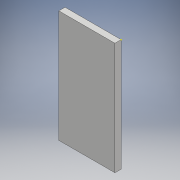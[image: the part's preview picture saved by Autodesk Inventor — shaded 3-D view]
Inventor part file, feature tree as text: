
AUTODESK INVENTOR PART (.ipt)
format: ipt  version: 2017 SP1 (Build 210196100, 196)  size: 90,112 bytes
history: native  units: mm
features: sketch x2, extrude x1
ambient origin geometry x8: Origin, YZ Plane, XZ Plane, XY Plane, X Axis, Y Axis, Z Axis, Center Point
bodies: Solide1 (feature_tree)
feature tree (3):
  extrude  "Extrusion1"  Depth=90.0mm
  sketch  "Esquisse2"
  sketch  "Esquisse1"
